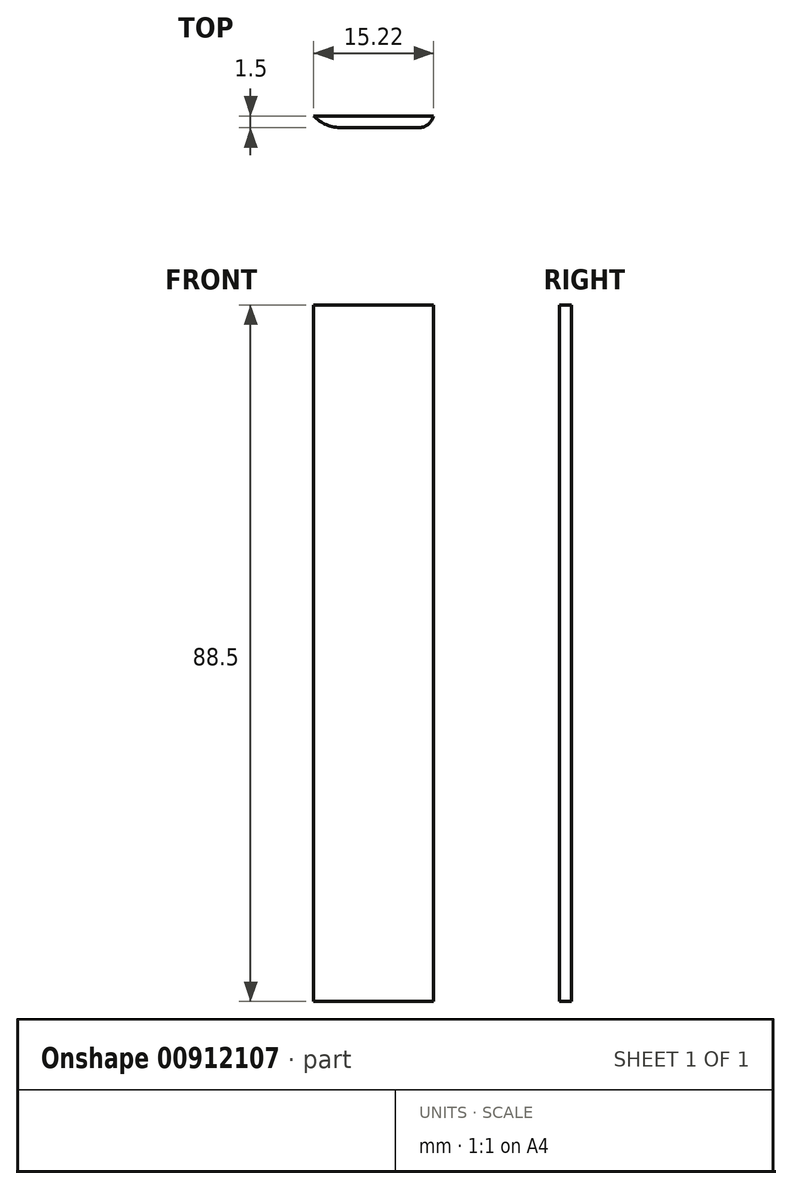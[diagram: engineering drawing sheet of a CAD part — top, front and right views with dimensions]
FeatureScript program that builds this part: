
annotation { "Feature Type Name" : "Feature", "Feature Type Description" : "" }
export const myFeature = defineFeature(function(context is Context, id is Id, definition is map)
    precondition{}
    {
        {
            var Q0;
            Q0=qCreatedBy(makeId("Front.planeOp"),FACE);
            var sketch = newSketch(context, id + "F0", { "sketchPlane" : qUnion([Q0])});
            skLineSegment(sketch, "E0.bottom", {"start": v(-63.35, 54.94) * mm, "end": v(92.65, 54.94) * mm});
            skLineSegment(sketch, "E0.top", {"start": v(-63.35, -33.56) * mm, "end": v(92.65, -33.56) * mm});
            skLineSegment(sketch, "E0.left", {"start": v(-63.35, 54.94) * mm, "end": v(-63.35, -33.56) * mm});
            skLineSegment(sketch, "E0.right", {"start": v(92.65, 54.94) * mm, "end": v(92.65, -33.56) * mm});
            skLineSegment(sketch, "E1.bottom", {"start": v(-63.35, 54.94) * mm, "end": v(92.43, 54.94) * mm});
            skLineSegment(sketch, "E1.top", {"start": v(-63.35, 69.94) * mm, "end": v(92.65, 69.94) * mm});
            skLineSegment(sketch, "E2.top", {"start": v(-63.57, -48.56) * mm, "end": v(92.65, -48.56) * mm});
            skLineSegment(sketch, "E3.bottom", {"start": v(-63.35, 69.94) * mm, "end": v(-78.57, 69.94) * mm});
            skLineSegment(sketch, "E3.top", {"start": v(-63.35, -48.56) * mm, "end": v(-78.57, -48.56) * mm});
            skLineSegment(sketch, "E3.right", {"start": v(-78.57, 69.94) * mm, "end": v(-78.57, -48.56) * mm});
            skLineSegment(sketch, "E4.bottom", {"start": v(92.65, 69.94) * mm, "end": v(107.43, 69.94) * mm});
            skLineSegment(sketch, "E4.top", {"start": v(92.65, -48.56) * mm, "end": v(107.43, -48.56) * mm});
            skLineSegment(sketch, "E4.right", {"start": v(107.43, 69.94) * mm, "end": v(107.43, -48.56) * mm});
            skLineSegment(sketch, "E5", {"start": v(-63.35, 54.94) * mm, "end": v(-78.57, 54.94) * mm});
            skLineSegment(sketch, "E6", {"start": v(92.65, 54.94) * mm, "end": v(107.43, 54.94) * mm});
            skLineSegment(sketch, "E7", {"start": v(-63.35, -33.56) * mm, "end": v(-78.57, -33.56) * mm});
            skLineSegment(sketch, "E8", {"start": v(92.65, -33.56) * mm, "end": v(107.43, -33.56) * mm});
            skLineSegment(sketch, "E9.bottom", {"start": v(-78.57, 69.94) * mm, "end": v(107.42, 69.94) * mm});
            skLineSegment(sketch, "E9.left", {"start": v(-78.57, 69.94) * mm, "end": v(-78.57, 64.06) * mm});
            skLineSegment(sketch, "E9.right", {"start": v(107.42, 69.94) * mm, "end": v(107.42, 64.06) * mm});
            skLineSegment(sketch, "E10.bottom", {"start": v(-78.57, -48.56) * mm, "end": v(107.98, -48.56) * mm});
            skLineSegment(sketch, "E10.left", {"start": v(-78.57, -48.56) * mm, "end": v(-78.57, -40.41) * mm});
            skLineSegment(sketch, "E10.right", {"start": v(107.98, -48.56) * mm, "end": v(107.98, -40.41) * mm});
            skSolve(sketch);
        }
        {
            var Q0;
            Q0=makeQuery(id+"F0.imprint","IMPRINT",FACE,{"disambiguationData":[TD([[makeQuery(id+"F0.imprint","IMPRINT",EDGE,{"derivedFrom":sQuery(id+"F0.wireOp",EDGE,"E0.left")}),-1.0]])]});
            var Q1;
            Q1=makeQuery(id+"F0.imprint","IMPRINT",FACE,{"disambiguationData":[TD([[makeQuery(id+"F0.imprint","IMPRINT",EDGE,{"derivedFrom":sQuery(id+"F0.wireOp",EDGE,"E0.right")}),1.0]])]});
            var Q2;
            Q2=makeQuery(id+"F0.imprint","IMPRINT",FACE,{"disambiguationData":[TD([[makeQuery(id+"F0.imprint","IMPRINT",EDGE,{"derivedFrom":sQuery(id+"F0.wireOp",EDGE,"E1.bottom")}),1.0]])]});
            var Q3;
            Q3=makeQuery(id+"F0.imprint","IMPRINT",FACE,{"disambiguationData":[TD([[makeQuery(id+"F0.imprint","IMPRINT",EDGE,{"derivedFrom":sQuery(id+"F0.wireOp",EDGE,"E0.top")}),-1.0]])]});
            extrude(context, id + "F1", {"entities" : qUnion([Q0, Q1, Q2, Q3]), "depth" : 1.5 * mm, "offsetDistance" : 25 * mm});
        }
        {
            var Q0;
            Q0=makeQuery(id+"F1.opExtrude","CAP_EDGE",EDGE,{"disambiguationData":[OSD([sQuery(id+"F0.wireOp",EDGE,"E0.left")])],"isStart":false});
            var Q1;
            Q1=makeQuery(id+"F1.opExtrude","CAP_EDGE",EDGE,{"disambiguationData":[OSD([sQuery(id+"F0.wireOp",EDGE,"E1.bottom")])],"isStart":false});
            var Q2;
            Q2=makeQuery(id+"F1.opExtrude","CAP_EDGE",EDGE,{"disambiguationData":[OSD([sQuery(id+"F0.wireOp",EDGE,"E0.right")])],"isStart":false});
            var Q3;
            Q3=makeQuery(id+"F1.opExtrude","CAP_EDGE",EDGE,{"disambiguationData":[OSD([sQuery(id+"F0.wireOp",EDGE,"E0.top")])],"isStart":false});
            fillet(context, id + "F2", {"entities" : qUnion([Q0, Q1, Q2, Q3]), "radius" : 2 * mm, "tangentPropagation" : true, "allowEdgeOverflow" : false});
        }
        {
            var Q0;
            Q0=makeQuery(id+"F1.opExtrude","CAP_EDGE",EDGE,{"disambiguationData":[OSD([sQuery(id+"F0.wireOp",EDGE,"E9.bottom")])],"isStart":false});
            var Q1;
            Q1=makeQuery(id+"F1.opExtrude","CAP_EDGE",EDGE,{"disambiguationData":[OSD([sQuery(id+"F0.wireOp",EDGE,"E4.right")])],"isStart":false});
            var Q2;
            Q2=makeQuery(id+"F1.opExtrude","CAP_EDGE",EDGE,{"disambiguationData":[OSD([sQuery(id+"F0.wireOp",EDGE,"E10.bottom")])],"isStart":false});
            var Q3;
            Q3=makeQuery(id+"F1.opExtrude","CAP_EDGE",EDGE,{"disambiguationData":[OSD([sQuery(id+"F0.wireOp",EDGE,"E3.right"),sQuery(id+"F0.wireOp",EDGE,"E9.left"),sQuery(id+"F0.wireOp",EDGE,"E10.left")])],"isStart":false});
            fillet(context, id + "F3", {"entities" : qUnion([Q0, Q1, Q2, Q3]), "radius" : 5 * mm, "tangentPropagation" : true, "allowEdgeOverflow" : false});
        }
    });
